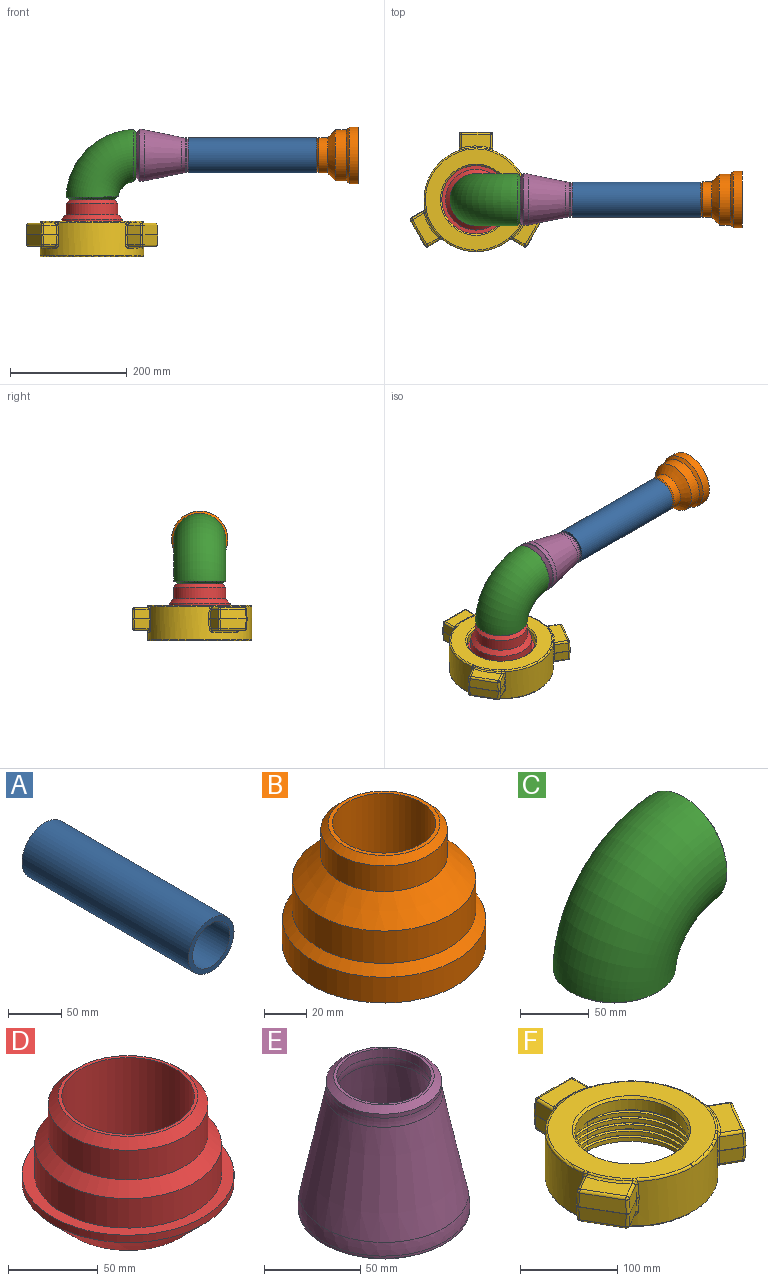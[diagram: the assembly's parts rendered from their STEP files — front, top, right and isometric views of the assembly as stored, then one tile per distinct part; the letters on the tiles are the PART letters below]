
ASSEMBLY  parts=6 mates=5
PART A: 4 faces, bbox 60.3x220x60.3 mm
  f0: cylinder r=24.61mm len=220mm, axis (0,1,0), area 34018.4mm2, adj f2,f3
  f1: cylinder r=30.15mm len=220mm, axis (0,1,0), area 41676.4mm2, adj f2,f3
  f2: plane 60.3x60.3mm, normal (0,-1,0), area 953.1mm2, adj f0,f1
  f3: plane 60.3x60.3mm, normal (0,1,0), area 953.1mm2, adj f0,f1
PART B: 11 faces, bbox 96.8x96.8x70.6 mm
  f0: cylinder r=24.61mm len=66.04mm, axis (0,0,1), area 10211.3mm2, adj f1,f10
  f1: plane 53.22x53.22mm, normal (0,0,1), area 321.8mm2, adj f0,f2
  f2: cone r=26.61mm half-angle=45deg, axis (0,0,-1), area 892.7mm2, adj f1,f3
  f3: cylinder r=30.15mm len=60.3mm, axis (0,0,1), area 2841.6mm2, adj f2,f4
  f4: cone r=30.15mm half-angle=45deg, axis (0,0,-1), area 4426.4mm2, adj f3,f5
  f5: cylinder r=43.65mm len=87.3mm, axis (0,0,1), area 5158.9mm2, adj f4,f6
  f6: cone r=43.65mm half-angle=45deg, axis (0,0,-1), area 1942.6mm2, adj f5,f7
  f7: cylinder r=48.4mm len=96.8mm, axis (0,0,1), area 4561.6mm2, adj f6,f8
  f8: plane 96.8x96.8mm, normal (0,0,-1), area 2620.7mm2, adj f7,f9
  f9: cylinder r=38.84mm len=77.68mm, axis (0,0,1), area 1113.4mm2, adj f8,f10
  f10: plane 77.68x77.68mm, normal (0,0,-1), area 2835.9mm2, adj f0,f9
PART C: 6 faces, bbox 130.3x89.8x130.3 mm
  f0: torus R=76mm, axis (0,-1,0), area 30764.5mm2, adj f1,f2
  f1: cone r=0mm half-angle=52.5deg, axis (0,0,1), area 2001.1mm2, adj f0,f5
  f2: cone r=0mm half-angle=52.5deg, axis (-1,0,0), area 2001.1mm2, adj f0,f3
  f3: plane 76.96x76.96mm, normal (1,0,0), area 378.8mm2, adj f2,f4
  f4: torus R=76mm, axis (0,-1,0), area 27663.3mm2, adj f3,f5
  f5: plane 76.96x76.96mm, normal (0,0,-1), area 378.8mm2, adj f1,f4
PART D: 11 faces, bbox 117.9x117.9x76.2 mm
  f0: cylinder r=36.83mm len=74.79mm, axis (0,0,1), area 17306.2mm2, adj f1,f10
  f1: plane 77.66x77.66mm, normal (0,0,1), area 475.4mm2, adj f0,f2
  f2: cone r=38.83mm half-angle=45deg, axis (0,0,-1), area 2079.4mm2, adj f1,f3
  f3: cylinder r=44.45mm len=88.9mm, axis (0,0,1), area 5585.8mm2, adj f2,f4
  f4: cone r=44.45mm half-angle=45deg, axis (0,0,-1), area 3230.7mm2, adj f3,f5
  f5: cylinder r=51.99mm len=103.98mm, axis (0,0,1), area 6533.3mm2, adj f4,f6
  f6: plane 117.87x117.87mm, normal (0,0,1), area 2420.2mm2, adj f5,f7
  f7: cylinder r=58.94mm len=117.87mm, axis (0,0,1), area 1851.5mm2, adj f6,f8
  f8: cone r=58.94mm half-angle=45deg, axis (0,0,1), area 8001.3mm2, adj f7,f9
  f9: plane 81.79x81.79mm, normal (0,0,-1), area 659mm2, adj f8,f10
  f10: cone r=38.24mm half-angle=45deg, axis (0,0,-1), area 471.7mm2, adj f0,f9
PART E: 14 faces, bbox 89x89x102.6 mm
  f0: plane 52.12x52.12mm, normal (0,0,1), area 253.9mm2, adj f1,f13
  f1: cylinder r=24.46mm len=48.92mm, axis (0,0,1), area 851.4mm2, adj f0,f2
  f2: torus R=51.46mm, axis (0,0,1), area 716.7mm2, adj f1,f3
  f3: cone r=0mm half-angle=9.8deg, axis (0,0,-1), area 12849.2mm2, adj f2,f4
  f4: revolved ~73.76x73.76mm, area 1585.7mm2, adj f3,f5
  f5: cylinder r=36.88mm len=73.76mm, axis (0,0,1), area 1412.6mm2, adj f4,f6
  f6: plane 76.96x76.96mm, normal (0,0,-1), area 378.8mm2, adj f5,f7
  f7: cone r=0mm half-angle=52.5deg, axis (0,0,1), area 1978.1mm2, adj f6,f8
  f8: cylinder r=44.5mm len=89mm, axis (0,0,1), area 412.9mm2, adj f7,f9
  f9: torus R=4.45mm, axis (0,0,1), area 2256.1mm2, adj f8,f10
  f10: cone r=0mm half-angle=11.6deg, axis (0,0,-1), area 15205.1mm2, adj f9,f11
  f11: torus R=57mm, axis (0,0,1), area 1038.1mm2, adj f10,f12
  f12: cylinder r=30mm len=60mm, axis (0,0,1), area 474.4mm2, adj f11,f13
  f13: cone r=0mm half-angle=52.5deg, axis (0,0,-1), area 874.6mm2, adj f0,f12
PART F: 157 faces, bbox 228x213.6x63.4 mm
  f0: cylinder r=64.58mm len=89.89mm, axis (0,0,-1), area 158.2mm2, adj f1,f3,f155
  f1: cylinder r=64.58mm len=129.16mm, axis (0,0,-1), area 855.4mm2, adj f0,f2,f3,f16,f155
  f2: bspline ~133.03x132.32mm, area 5844mm2, adj f1,f4,f15,f16,f17,f18,f19,f20
  f3: bspline ~133.9x133.85mm, area 5562.3mm2, adj f0,f1,f4,f16,f17,f18,f19,f20
  f4: cylinder r=67.12mm len=134.24mm, axis (0,0,-1), area 3300.1mm2, adj f2,f3,f25,f155
  f5: cylinder r=88.9mm len=177.8mm, axis (0,0,-1), area 23429mm2, adj f100,f101,f102,f103,f104,f105,f106,f107
  f6: cylinder r=3.17mm len=43.92mm, axis (0.5,0.87,0), area 16.9mm2, adj f9,f10,f11,f13
  f7: cylinder r=3.17mm len=50.71mm, axis (-1,0,0), area 16.9mm2, adj f12,f26,f27,f52
  f8: cylinder r=3.17mm len=43.92mm, axis (0.5,-0.87,0), area 16.9mm2, adj f14,f28,f29,f30
  f9: sphere r=3.17mm, area 2.2mm2, adj f6,f31,f32,f64
  f10: plane 43.92x25.68mm, normal (0.86,-0.5,-0.05), area 831.9mm2, adj f6,f32,f34,f36
  f11: sphere r=3.17mm, area 2.1mm2, adj f6,f36,f37,f70
  f12: sphere r=3.17mm, area 2.1mm2, adj f7,f38,f39,f73
  f13: plane 43.92x25.68mm, normal (0.86,-0.5,0.05), area 831.9mm2, adj f6,f31,f37,f42
  f14: plane 43.92x25.68mm, normal (-0.86,-0.5,0.05), area 831.9mm2, adj f8,f48,f56,f62
  f15: cylinder r=64.58mm len=129.16mm, axis (0,0,-1), area 927.5mm2, adj f2,f24,f46
  f16: cylinder r=64.58mm len=129.16mm, axis (0,0,-1), area 1025.4mm2, adj f1,f2,f3,f17
  f17: cylinder r=64.58mm len=129.16mm, axis (0,0,-1), area 1025.4mm2, adj f2,f3,f16,f18
  f18: cylinder r=64.58mm len=129.16mm, axis (0,0,-1), area 1025.4mm2, adj f2,f3,f17,f19
  f19: cylinder r=64.58mm len=129.16mm, axis (0,0,-1), area 1025.4mm2, adj f2,f3,f18,f20
  f20: cylinder r=64.58mm len=129.16mm, axis (0,0,-1), area 1025.4mm2, adj f2,f3,f19,f21
  f21: cylinder r=64.58mm len=129.16mm, axis (0,0,-1), area 1025.4mm2, adj f2,f3,f20,f22
  f22: cylinder r=64.58mm len=129.16mm, axis (0,0,-1), area 1025.4mm2, adj f2,f3,f21,f23
  f23: cylinder r=64.58mm len=129.16mm, axis (0,0,-1), area 1025.4mm2, adj f2,f3,f22,f24
  f24: cylinder r=64.58mm len=129.16mm, axis (0,0,-1), area 1439.7mm2, adj f2,f3,f15,f23,f25,f47
  f25: plane 2.84x2.54mm, normal (0,1,0), area 5.5mm2, adj f2,f3,f4,f24
  f26: plane 50.71x16.67mm, normal (0,1,-0.05), area 831.9mm2, adj f7,f39,f49,f51
  f27: plane 50.71x16.67mm, normal (0,1,0.05), area 831.9mm2, adj f7,f38,f45,f53
  f28: sphere r=3.17mm, area 2.1mm2, adj f8,f56,f57,f92
  f29: plane 43.92x25.68mm, normal (-0.86,-0.5,-0.05), area 831.9mm2, adj f8,f57,f59,f61
  f30: sphere r=3.17mm, area 2.2mm2, adj f8,f61,f62,f98
  f31: cylinder r=3.17mm len=16.74mm, axis (-0.02,0.07,1), area 83.2mm2, adj f9,f13,f41,f63
  f32: cylinder r=3.17mm len=16.74mm, axis (-0.02,0.07,-1), area 83.2mm2, adj f9,f10,f33,f65
  f33: sphere r=3.17mm, area 11mm2, adj f32,f34,f66
  f34: cylinder r=3.17mm len=43.99mm, axis (0.5,0.87,0), area 236.1mm2, adj f10,f33,f35,f67
  f35: sphere r=3.17mm, area 15.4mm2, adj f34,f36,f68
  f36: cylinder r=3.17mm len=16.74mm, axis (-0.07,-0.02,-1), area 83.2mm2, adj f10,f11,f35,f69
  f37: cylinder r=3.17mm len=16.74mm, axis (-0.07,-0.02,1), area 83.2mm2, adj f11,f13,f43,f71
  f38: cylinder r=3.17mm len=16.74mm, axis (-0.05,-0.05,1), area 83.2mm2, adj f12,f27,f44,f72
  f39: cylinder r=3.17mm len=16.74mm, axis (-0.05,-0.05,-1), area 83.2mm2, adj f12,f26,f40,f74
  f40: sphere r=3.17mm, area 9.6mm2, adj f39,f49,f75
  f41: sphere r=3.17mm, area 13.7mm2, adj f31,f42,f76
  f42: cylinder r=3.17mm len=43.99mm, axis (0.5,0.87,0), area 236.1mm2, adj f13,f41,f43,f77
  f43: sphere r=3.17mm, area 10mm2, adj f37,f42,f78
  f44: sphere r=3.17mm, area 9.6mm2, adj f38,f45,f79
  f45: cylinder r=3.17mm len=48.97mm, axis (-1,0,0), area 236.1mm2, adj f27,f44,f54,f80
  f46: torus R=63.31mm, axis (0,0,-1), area 401.8mm2, adj f15,f47,f81
  f47: torus R=63.31mm, axis (0,0,-1), area 401.8mm2, adj f24,f46,f81
  f48: cylinder r=3.17mm len=43.99mm, axis (0.5,-0.87,0), area 236.1mm2, adj f14,f55,f82,f83
  f49: cylinder r=3.17mm len=48.97mm, axis (-1,0,0), area 236.1mm2, adj f26,f40,f50,f84
  f50: sphere r=3.17mm, area 9.6mm2, adj f49,f51,f85
  f51: cylinder r=3.17mm len=16.74mm, axis (0.05,-0.05,-1), area 83.2mm2, adj f26,f50,f52,f86
  f52: revolved ~6.35x3.18mm, area 2.1mm2, adj f7,f51,f53,f87
  f53: cylinder r=3.17mm len=16.74mm, axis (0.05,-0.05,1), area 83.2mm2, adj f27,f52,f54,f88
  f54: sphere r=3.17mm, area 9.6mm2, adj f45,f53,f89
  f55: sphere r=3.17mm, area 15.4mm2, adj f48,f56,f90
  f56: cylinder r=3.17mm len=16.74mm, axis (0.07,-0.02,1), area 83.2mm2, adj f14,f28,f55,f91
  f57: cylinder r=3.17mm len=16.74mm, axis (0.07,-0.02,-1), area 83.2mm2, adj f28,f29,f58,f93
  f58: sphere r=3.17mm, area 10mm2, adj f57,f59,f94
  f59: cylinder r=3.17mm len=43.99mm, axis (0.5,-0.87,0), area 236.1mm2, adj f29,f58,f60,f95
  f60: sphere r=3.17mm, area 11mm2, adj f59,f61,f96
  f61: cylinder r=3.17mm len=16.74mm, axis (0.02,0.07,-1), area 83.2mm2, adj f29,f30,f60,f97
  f62: cylinder r=3.17mm len=16.74mm, axis (0.02,0.07,1), area 83.2mm2, adj f14,f30,f82,f99
  f63: plane 22.27x16.67mm, normal (-0.5,-0.86,0.05), area 419.3mm2, adj f31,f64,f76,f100
  f64: cylinder r=3.17mm len=22.27mm, axis (0.87,-0.5,0), area 8.5mm2, adj f9,f63,f65,f101
  f65: plane 22.27x16.67mm, normal (-0.5,-0.86,-0.05), area 419.3mm2, adj f32,f64,f66,f102
  f66: cylinder r=3.17mm len=22.82mm, axis (0.87,-0.5,0), area 113.4mm2, adj f33,f65,f67,f103
  f67: plane 53.77x44.1mm, normal (0,0,-1), area 994.3mm2, adj f34,f66,f68,f104
  f68: cylinder r=3.17mm len=22.82mm, axis (-0.87,0.5,0), area 113.4mm2, adj f35,f67,f69,f105
  f69: plane 22.43x16.67mm, normal (0.5,0.86,-0.05), area 419.3mm2, adj f36,f68,f70,f106
  f70: cylinder r=3.17mm len=22.27mm, axis (-0.87,0.5,0), area 8.5mm2, adj f11,f69,f71,f107
  f71: plane 22.43x16.67mm, normal (0.5,0.86,0.05), area 419.3mm2, adj f37,f70,f78,f108
  f72: plane 25.71x16.67mm, normal (1,0,0.05), area 419.3mm2, adj f38,f73,f79,f109
  f73: cylinder r=3.17mm len=25.71mm, axis (0,1,0), area 8.5mm2, adj f12,f72,f74,f110
  f74: plane 25.71x16.67mm, normal (1,0,-0.05), area 419.3mm2, adj f39,f73,f75,f111
  f75: cylinder r=3.17mm len=24.52mm, axis (0,1,0), area 113.4mm2, adj f40,f74,f84,f112
  f76: cylinder r=3.17mm len=22.82mm, axis (0.87,-0.5,0), area 113.4mm2, adj f41,f63,f77,f114
  f77: plane 53.77x44.1mm, normal (0,0,1), area 994.3mm2, adj f42,f76,f78,f115
  f78: cylinder r=3.17mm len=22.82mm, axis (-0.87,0.5,0), area 113.4mm2, adj f43,f71,f77,f116
  f79: cylinder r=3.17mm len=24.52mm, axis (0,1,0), area 113.4mm2, adj f44,f72,f80,f117
  f80: plane 49.07x22.63mm, normal (0,0,1), area 994.3mm2, adj f45,f79,f89,f118
  f81: plane 126.62x126.62mm, normal (0,0,-1), area 1866.7mm2, adj f46,f47,f119
  f82: sphere r=3.17mm, area 13.7mm2, adj f48,f62,f120
  f83: plane 53.77x44.1mm, normal (0,0,1), area 994.3mm2, adj f48,f90,f120,f121
  f84: plane 48.97x22.53mm, normal (0,0,-1), area 994.4mm2, adj f49,f75,f85,f113,f122
  f85: cylinder r=3.17mm len=24.52mm, axis (0,-1,0), area 113.4mm2, adj f50,f84,f86,f123
  f86: plane 25.71x16.67mm, normal (-1,0,-0.05), area 419.3mm2, adj f51,f85,f87,f124
  f87: cylinder r=3.17mm len=25.71mm, axis (0,-1,0), area 8.5mm2, adj f52,f86,f88,f125
  f88: plane 25.71x16.67mm, normal (-1,0,0.05), area 419.3mm2, adj f53,f87,f89,f126
  f89: cylinder r=3.17mm len=24.52mm, axis (0,-1,0), area 113.4mm2, adj f54,f80,f88,f127
  f90: cylinder r=3.17mm len=22.82mm, axis (-0.87,-0.5,0), area 113.4mm2, adj f55,f83,f91,f128
  f91: plane 22.43x16.67mm, normal (-0.5,0.86,0.05), area 419.3mm2, adj f56,f90,f92,f129
  f92: cylinder r=3.17mm len=22.27mm, axis (-0.87,-0.5,0), area 8.5mm2, adj f28,f91,f93,f130
  f93: plane 22.43x16.67mm, normal (-0.5,0.86,-0.05), area 419.3mm2, adj f57,f92,f94,f131
  f94: cylinder r=3.17mm len=22.82mm, axis (-0.87,-0.5,0), area 113.4mm2, adj f58,f93,f95,f132
  f95: plane 53.77x44.1mm, normal (0,0,-1), area 994.3mm2, adj f59,f94,f96,f133
  f96: cylinder r=3.17mm len=22.82mm, axis (0.87,0.5,0), area 113.4mm2, adj f60,f95,f97,f134
  f97: plane 22.27x16.67mm, normal (0.5,-0.86,-0.05), area 419.3mm2, adj f61,f96,f98,f135
  f98: cylinder r=3.17mm len=22.27mm, axis (0.87,0.5,0), area 8.5mm2, adj f30,f97,f99,f136
  f99: plane 22.27x16.67mm, normal (0.5,-0.86,0.05), area 419.3mm2, adj f62,f98,f120,f137
  f100: bspline ~16.84x4.33mm, area 64.9mm2, adj f5,f63,f101,f114
  f101: bspline ~3.63x1.43mm, area 1.8mm2, adj f5,f64,f100,f102
  f102: bspline ~16.84x4.33mm, area 64.9mm2, adj f5,f65,f101,f103
  f103: bspline ~6.96x6.18mm, area 30.2mm2, adj f5,f66,f102,f104
  f104: torus R=92.08mm, axis (0,0,-1), area 241.7mm2, adj f5,f67,f103,f105
  f105: bspline ~7.07x6.18mm, area 30.2mm2, adj f5,f68,f104,f106
  f106: bspline ~16.84x4.2mm, area 64.9mm2, adj f5,f69,f105,f107
  f107: bspline ~3.3x1.92mm, area 1.8mm2, adj f5,f70,f106,f108
  f108: bspline ~16.84x4.2mm, area 64.9mm2, adj f5,f71,f107,f116
  f109: bspline ~16.84x3.3mm, area 64.9mm2, adj f5,f72,f110,f117
  f110: bspline ~2.99x2.09mm, area 1.8mm2, adj f5,f73,f109,f111
  f111: bspline ~16.84x3.3mm, area 64.9mm2, adj f5,f74,f110,f112
  f112: bspline ~6.18x6.12mm, area 30.2mm2, adj f5,f75,f111,f113
  f113: torus R=92.07mm, axis (0,0,-1), area 120.9mm2, adj f5,f84,f112,f122
  f114: bspline ~6.96x6.18mm, area 26.5mm2, adj f5,f76,f100,f115,f140
  f115: torus R=92.08mm, axis (0,0,1), area 171.7mm2, adj f77,f114,f116,f141
  f116: bspline ~7.07x6.18mm, area 26.5mm2, adj f5,f78,f108,f115,f142
  f117: bspline ~6.18x6.12mm, area 26.5mm2, adj f5,f79,f109,f118,f144
  f118: torus R=92.08mm, axis (0,0,1), area 171.7mm2, adj f80,f117,f127,f145,f146
  f119: cylinder r=58.42mm len=116.84mm, axis (0,0,1), area 4941.4mm2, adj f81,f148
  f120: cylinder r=3.17mm len=22.82mm, axis (0.87,0.5,0), area 113.4mm2, adj f82,f83,f99,f150
  f121: torus R=92.08mm, axis (0,0,1), area 171.7mm2, adj f83,f128,f149,f150
  f122: torus R=92.07mm, axis (0,0,-1), area 120.9mm2, adj f5,f84,f113,f123
  f123: bspline ~6.18x6.12mm, area 30.2mm2, adj f5,f85,f122,f124
  f124: bspline ~16.84x3.3mm, area 64.9mm2, adj f5,f86,f123,f125
  f125: bspline ~2.99x2.09mm, area 1.8mm2, adj f5,f87,f124,f126
  f126: bspline ~16.84x3.3mm, area 64.9mm2, adj f5,f88,f125,f127
  f127: bspline ~6.18x6.12mm, area 26.5mm2, adj f5,f89,f118,f126,f147
  f128: bspline ~7.07x6.18mm, area 26.5mm2, adj f5,f90,f121,f129,f139
  f129: bspline ~16.84x4.2mm, area 64.9mm2, adj f5,f91,f128,f130
  f130: bspline ~3.3x1.92mm, area 1.8mm2, adj f5,f92,f129,f131
  f131: bspline ~16.84x4.2mm, area 64.9mm2, adj f5,f93,f130,f132
  f132: bspline ~7.07x6.18mm, area 30.2mm2, adj f5,f94,f131,f133
  f133: torus R=92.08mm, axis (0,0,-1), area 241.7mm2, adj f5,f95,f132,f134
  f134: bspline ~6.96x6.18mm, area 30.2mm2, adj f5,f96,f133,f135
  f135: bspline ~16.84x4.33mm, area 64.9mm2, adj f5,f97,f134,f136
  f136: bspline ~3.63x1.43mm, area 1.8mm2, adj f5,f98,f135,f137
  f137: bspline ~16.84x4.33mm, area 64.9mm2, adj f5,f99,f136,f150
  f138: torus R=86.36mm, axis (0,0,1), area 505.7mm2, adj f5,f139,f147,f152
  f139: bspline ~5.58x3.03mm, area 16.8mm2, adj f128,f138,f149,f152
  f140: bspline ~5.66x4.88mm, area 16.8mm2, adj f114,f141,f151,f152
  f141: torus R=86.96mm, axis (0,0,-1), area 133.9mm2, adj f115,f140,f142,f152
  f142: bspline ~5.58x3.03mm, area 16.8mm2, adj f116,f141,f143,f152
  f143: torus R=86.36mm, axis (0,0,1), area 505.7mm2, adj f5,f142,f144,f152
  f144: bspline ~5.42x4.23mm, area 16.8mm2, adj f117,f143,f145,f152
  f145: torus R=86.96mm, axis (0,0,-1), area 67mm2, adj f118,f144,f146,f152
  f146: torus R=86.96mm, axis (0,0,-1), area 67mm2, adj f118,f145,f147,f152
  f147: bspline ~5.42x4.23mm, area 16.8mm2, adj f127,f138,f146,f152
  f148: cone r=0mm half-angle=45deg, axis (0,0,1), area 1347.2mm2, adj f119,f152
  f149: torus R=86.96mm, axis (0,0,-1), area 133.9mm2, adj f121,f139,f152,f153
  f150: bspline ~6.96x6.18mm, area 26.5mm2, adj f5,f120,f121,f137,f153
  f151: torus R=86.36mm, axis (0,0,1), area 252.8mm2, adj f5,f140,f152,f154
  f152: plane 175.35x175.01mm, normal (0,0,1), area 11842.4mm2, adj f138,f139,f140,f141,f142,f143,f144,f145
  f153: bspline ~5.66x4.88mm, area 16.8mm2, adj f149,f150,f152,f154
  f154: torus R=86.36mm, axis (0,0,1), area 252.8mm2, adj f5,f151,f152,f153
  f155: plane 174.07x174.07mm, normal (0,0,-1), area 10332.2mm2, adj f0,f1,f2,f3,f4,f156
  f156: torus R=86.9mm, axis (0,0,-1), area 1740.5mm2, adj f5,f155
PLACE A rot(axis=(-0.58,-0.58,-0.58),120deg) t=(363.56,2.58,24.56)mm
PLACE B rot(axis=(-0.58,-0.58,0.58),120deg) t=(396.58,2.58,24.56)mm
PLACE C t=(-21.44,2.58,-51.44)mm fixed
PLACE D t=(-21.44,2.58,-88.83)mm
PLACE E rot(axis=(0.71,0,0.71),180deg) t=(54.56,2.58,24.56)mm
PLACE F t=(-21.44,2.58,-159.21)mm
MATE slider F.f0 <-> D.f0  axis (0,0,-1) through (-21.44,2.58,-104.6)mm
MATE slider A.f1 <-> B.f0  axis (1,0,0) through (363.56,2.58,24.56)mm
MATE slider D.f0 <-> C.f1  axis (0,0,1) through (-21.44,2.58,-51.44)mm
MATE slider B.f0 <-> E.f1  axis (1,0,0) through (434.16,2.58,24.56)mm
MATE slider E.f9 <-> C.f2  axis (-1,0,0) through (54.56,2.58,24.56)mm
